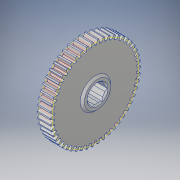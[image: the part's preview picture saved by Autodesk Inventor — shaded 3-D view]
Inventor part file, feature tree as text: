
AUTODESK INVENTOR PART (.ipt)
format: ipt  version: 2018 (Build 220112000, 112)  size: 358,400 bytes
history: native  units: in
note: dims shown in document units (in); Inventor stores cm internally (conversion verified against a paired STEP export)
features: other x3, sketch x1
ambient origin geometry x8: Origin, YZ Plane, XZ Plane, XY Plane, X Axis, Y Axis, Z Axis, Center Point
bodies: Solid1 (feature_tree)
feature tree (4):
  sketch  "Sketch1"  dims[d0=2.5in d1=1.0in d2=0.0in]
  other  "Srf1"
  other  "Cut-Extrude3"
  other  "pitch circle"
